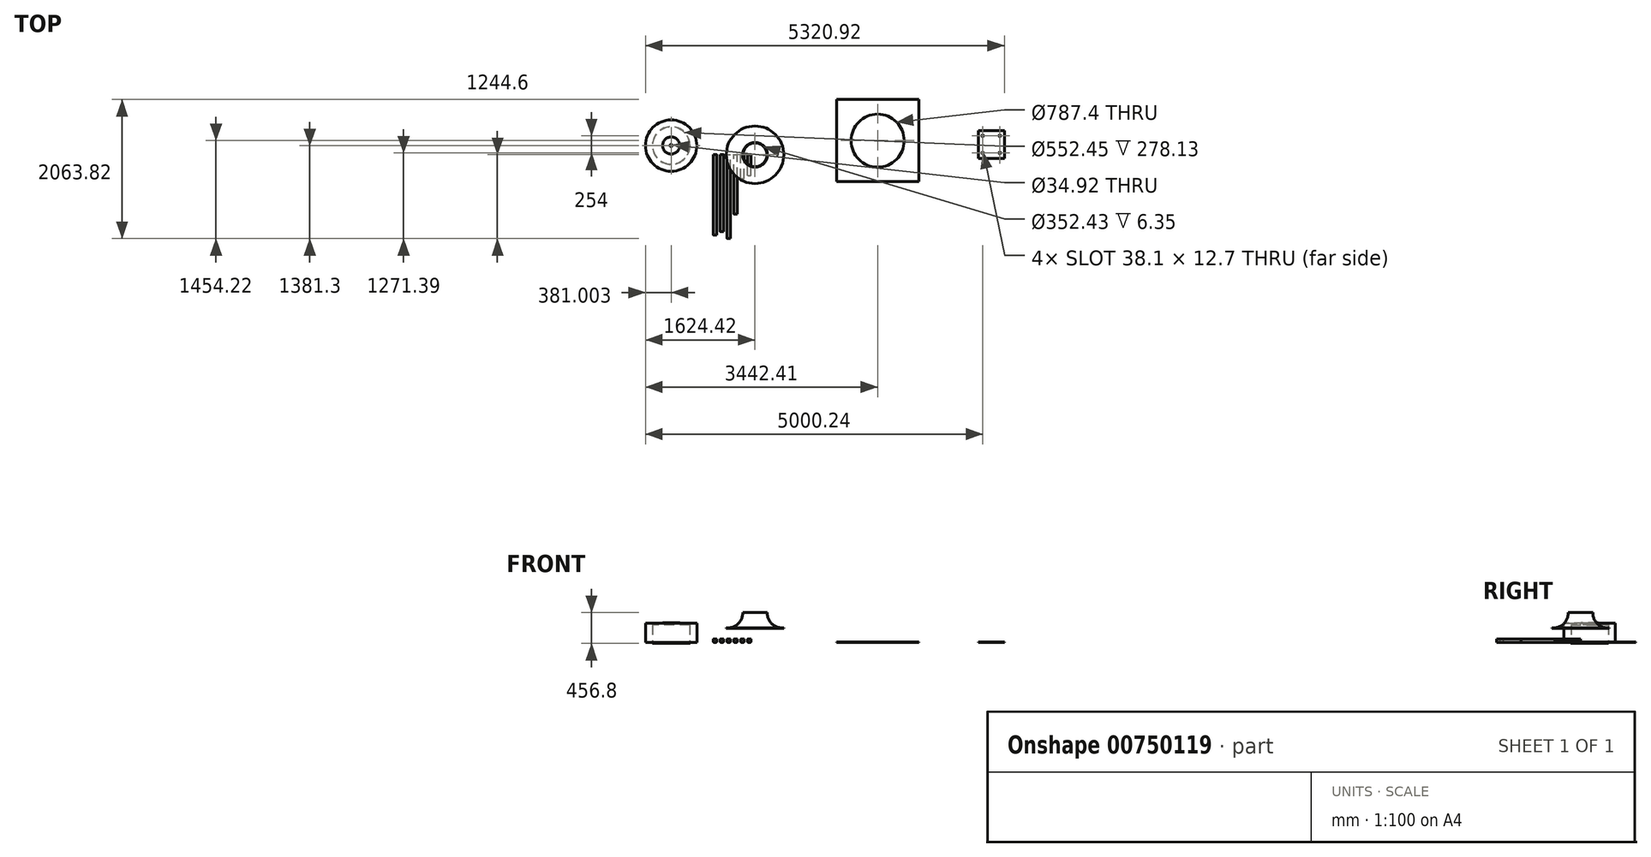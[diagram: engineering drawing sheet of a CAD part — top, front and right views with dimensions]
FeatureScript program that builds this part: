
annotation { "Feature Type Name" : "Feature", "Feature Type Description" : "" }
export const myFeature = defineFeature(function(context is Context, id is Id, definition is map)
    precondition{}
    {
        {
            var Q0;
            Q0=qCreatedBy(makeId("Front.planeOp"),FACE);
            var sketch = newSketch(context, id + "F0", { "sketchPlane" : qUnion([Q0])});
            skLineSegment(sketch, "E0.bottom", {"start": v(0, 0) * mm, "end": v(50.8, 0) * mm});
            skLineSegment(sketch, "E0.top", {"start": v(0, 50.8) * mm, "end": v(50.8, 50.8) * mm});
            skLineSegment(sketch, "E0.left", {"start": v(0, 0) * mm, "end": v(0, 50.8) * mm});
            skLineSegment(sketch, "E0.right", {"start": v(50.8, 0) * mm, "end": v(50.8, 50.8) * mm});
            skLineSegment(sketch, "E1.1.0.0", {"start": v(101.6, 0) * mm, "end": v(101.6, 50.8) * mm});
            skLineSegment(sketch, "E1.1.0.1", {"start": v(101.6, 50.8) * mm, "end": v(152.4, 50.8) * mm});
            skLineSegment(sketch, "E1.1.0.2", {"start": v(152.4, 0) * mm, "end": v(152.4, 50.8) * mm});
            skLineSegment(sketch, "E1.1.0.3", {"start": v(101.6, 0) * mm, "end": v(152.4, 0) * mm});
            skLineSegment(sketch, "E1.2.0.0", {"start": v(203.2, 0) * mm, "end": v(203.2, 50.8) * mm});
            skLineSegment(sketch, "E1.2.0.1", {"start": v(203.2, 50.8) * mm, "end": v(254, 50.8) * mm});
            skLineSegment(sketch, "E1.2.0.2", {"start": v(254, 0) * mm, "end": v(254, 50.8) * mm});
            skLineSegment(sketch, "E1.2.0.3", {"start": v(203.2, 0) * mm, "end": v(254, 0) * mm});
            skLineSegment(sketch, "E1.3.0.0", {"start": v(304.8, 0) * mm, "end": v(304.8, 50.8) * mm});
            skLineSegment(sketch, "E1.3.0.1", {"start": v(304.8, 50.8) * mm, "end": v(355.6, 50.8) * mm});
            skLineSegment(sketch, "E1.3.0.2", {"start": v(355.6, 0) * mm, "end": v(355.6, 50.8) * mm});
            skLineSegment(sketch, "E1.3.0.3", {"start": v(304.8, 0) * mm, "end": v(355.6, 0) * mm});
            skLineSegment(sketch, "E1.4.0.0", {"start": v(406.4, 0) * mm, "end": v(406.4, 50.8) * mm});
            skLineSegment(sketch, "E1.4.0.1", {"start": v(406.4, 50.8) * mm, "end": v(457.2, 50.8) * mm});
            skLineSegment(sketch, "E1.4.0.2", {"start": v(457.2, 0) * mm, "end": v(457.2, 50.8) * mm});
            skLineSegment(sketch, "E1.4.0.3", {"start": v(406.4, 0) * mm, "end": v(457.2, 0) * mm});
            skLineSegment(sketch, "E1.5.0.0", {"start": v(508, 0) * mm, "end": v(508, 50.8) * mm});
            skLineSegment(sketch, "E1.5.0.1", {"start": v(508, 50.8) * mm, "end": v(558.8, 50.8) * mm});
            skLineSegment(sketch, "E1.5.0.2", {"start": v(558.8, 0) * mm, "end": v(558.8, 50.8) * mm});
            skLineSegment(sketch, "E1.5.0.3", {"start": v(508, 0) * mm, "end": v(558.8, 0) * mm});
            skLineSegment(sketch, "E1.6.0.0", {"start": v(609.6, 0) * mm, "end": v(609.6, 50.8) * mm});
            skLineSegment(sketch, "E1.6.0.1", {"start": v(609.6, 50.8) * mm, "end": v(660.4, 50.8) * mm});
            skLineSegment(sketch, "E1.6.0.2", {"start": v(660.4, 0) * mm, "end": v(660.4, 50.8) * mm});
            skLineSegment(sketch, "E1.6.0.3", {"start": v(609.6, 0) * mm, "end": v(660.4, 0) * mm});
            skLineSegment(sketch, "E1.7.0.0", {"start": v(711.2, 0) * mm, "end": v(711.2, 50.8) * mm});
            skLineSegment(sketch, "E1.7.0.1", {"start": v(711.2, 50.8) * mm, "end": v(762, 50.8) * mm});
            skLineSegment(sketch, "E1.7.0.2", {"start": v(762, 0) * mm, "end": v(762, 50.8) * mm});
            skLineSegment(sketch, "E1.7.0.3", {"start": v(711.2, 0) * mm, "end": v(762, 0) * mm});
            skLineSegment(sketch, "E1.8.0.0", {"start": v(812.8, 0) * mm, "end": v(812.8, 50.8) * mm});
            skLineSegment(sketch, "E1.8.0.1", {"start": v(812.8, 50.8) * mm, "end": v(863.6, 50.8) * mm});
            skLineSegment(sketch, "E1.8.0.2", {"start": v(863.6, 0) * mm, "end": v(863.6, 50.8) * mm});
            skLineSegment(sketch, "E1.8.0.3", {"start": v(812.8, 0) * mm, "end": v(863.6, 0) * mm});
            skLineSegment(sketch, "E1.9.0.0", {"start": v(914.4, 0) * mm, "end": v(914.4, 50.8) * mm});
            skLineSegment(sketch, "E1.9.0.1", {"start": v(914.4, 50.8) * mm, "end": v(965.2, 50.8) * mm});
            skLineSegment(sketch, "E1.9.0.2", {"start": v(965.2, 0) * mm, "end": v(965.2, 50.8) * mm});
            skLineSegment(sketch, "E1.9.0.3", {"start": v(914.4, 0) * mm, "end": v(965.2, 0) * mm});
            skLineSegment(sketch, "E1.direction1", {"start": v(0, 0) * mm, "end": v(101.6, 0) * mm, "construction": true});
            skSolve(sketch);
        }
        {
            var Q0;
            Q0=makeQuery(id+"F0.imprint","IMPRINT",FACE,{"disambiguationData":[TD([[makeQuery(id+"F0.imprint","IMPRINT",EDGE,{"derivedFrom":sQuery(id+"F0.wireOp",EDGE,"E0.bottom")}),1.0]])]});
            extrude(context, id + "F1", {"entities" : qUnion([Q0]), "depth" : 1193.8 * mm, "offsetDistance" : 25.4 * mm});
        }
        {
            var Q0;
            Q0=makeQuery(id+"F1.opExtrude","SWEPT_EDGE",EDGE,{"disambiguationData":[OSD([sQuery(id+"F0.wireOp",EDGE,"E0.top"),sQuery(id+"F0.wireOp",EDGE,"E0.left")])]});
            var Q1;
            Q1=makeQuery(id+"F1.opExtrude","SWEPT_EDGE",EDGE,{"disambiguationData":[OSD([sQuery(id+"F0.wireOp",EDGE,"E0.bottom"),sQuery(id+"F0.wireOp",EDGE,"E0.left")])]});
            var Q2;
            Q2=makeQuery(id+"F1.opExtrude","SWEPT_EDGE",EDGE,{"disambiguationData":[OSD([sQuery(id+"F0.wireOp",EDGE,"E0.top"),sQuery(id+"F0.wireOp",EDGE,"E0.right")])]});
            var Q3;
            Q3=makeQuery(id+"F1.opExtrude","SWEPT_EDGE",EDGE,{"disambiguationData":[OSD([sQuery(id+"F0.wireOp",EDGE,"E0.bottom"),sQuery(id+"F0.wireOp",EDGE,"E0.right")])]});
            fillet(context, id + "F2", {"entities" : qUnion([Q0, Q1, Q2, Q3]), "radius" : 6.35 * mm, "tangentPropagation" : true, "allowEdgeOverflow" : false});
        }
        {
            var Q0;
            Q0=makeQuery(id+"F0.imprint","IMPRINT",FACE,{"disambiguationData":[TD([[makeQuery(id+"F0.imprint","IMPRINT",EDGE,{"derivedFrom":sQuery(id+"F0.wireOp",EDGE,"E1.1.0.0")}),-1.0]])]});
            extrude(context, id + "F3", {"entities" : qUnion([Q0]), "depth" : 1143 * mm, "offsetDistance" : 25.4 * mm});
        }
        {
            var Q0;
            Q0=makeQuery(id+"F0.imprint","IMPRINT",FACE,{"disambiguationData":[TD([[makeQuery(id+"F0.imprint","IMPRINT",EDGE,{"derivedFrom":sQuery(id+"F0.wireOp",EDGE,"E1.2.0.0")}),-1.0]])]});
            extrude(context, id + "F4", {"entities" : qUnion([Q0]), "depth" : 1244.6 * mm, "offsetDistance" : 25.4 * mm});
        }
        {
            var Q0;
            Q0=makeQuery(id+"F0.imprint","IMPRINT",FACE,{"disambiguationData":[TD([[makeQuery(id+"F0.imprint","IMPRINT",EDGE,{"derivedFrom":sQuery(id+"F0.wireOp",EDGE,"E1.3.0.0")}),-1.0]])]});
            extrude(context, id + "F5", {"entities" : qUnion([Q0]), "depth" : 882.65 * mm, "offsetDistance" : 25.4 * mm});
        }
        {
            var Q0;
            Q0=makeQuery(id+"F0.imprint","IMPRINT",FACE,{"disambiguationData":[TD([[makeQuery(id+"F0.imprint","IMPRINT",EDGE,{"derivedFrom":sQuery(id+"F0.wireOp",EDGE,"E1.4.0.0")}),-1.0]])]});
            extrude(context, id + "F6", {"entities" : qUnion([Q0]), "depth" : 355.6 * mm, "offsetDistance" : 25.4 * mm});
        }
        {
            var Q0;
            Q0=qCreatedBy(makeId("Front.planeOp"),FACE);
            var sketch = newSketch(context, id + "F7", { "sketchPlane" : qUnion([Q0])});
            skLineSegment(sketch, "E2", {"start": v(191.08, 213.6) * mm, "end": v(216.48, 213.6) * mm});
            skArc(sketch, "E3", {"start": v(216.48, 213.6) * mm, "mid": v(371.4, 277.76) * mm, "end": v(435.56, 432.67) * mm});
            skLineSegment(sketch, "E4", {"start": v(435.56, 432.67) * mm, "end": v(435.56, 439.02) * mm});
            skLineSegment(sketch, "E5", {"start": v(618.12, 554.37) * mm, "end": v(618.12, 107.04) * mm, "construction": true});
            skLineSegment(sketch, "E6.0", {"start": v(441.9, 432.67) * mm, "end": v(441.9, 439.02) * mm});
            skArc(sketch, "E6.1", {"start": v(216.48, 207.24) * mm, "mid": v(375.88, 273.27) * mm, "end": v(441.9, 432.67) * mm});
            skLineSegment(sketch, "E6.2", {"start": v(191.08, 207.24) * mm, "end": v(216.48, 207.24) * mm});
            skLineSegment(sketch, "E7", {"start": v(435.56, 439.02) * mm, "end": v(441.9, 439.02) * mm});
            skLineSegment(sketch, "E8", {"start": v(191.08, 213.6) * mm, "end": v(191.08, 207.24) * mm});
            skSolve(sketch);
        }
        {
            var Q0;
            Q0 = qSketchRegion(id + "F7", true);
            var Q1;
            Q1=sQuery(id+"F7.wireOp",EDGE,"E5");
            revolve(context, id + "F8", {"surfaceOperationType" : NewSurfaceOperationType.NEW, "entities" : qUnion([Q0]), "axis" : qUnion([Q1]), "revolveType" : RevolveType.FULL});
        }
        {
            var Q0;
            Q0=qCreatedBy(makeId("Top.planeOp"),FACE);
            var sketch = newSketch(context, id + "F9", { "sketchPlane" : qUnion([Q0])});
            skCircle(sketch, "E9", {"center": v(-625.3, 136.7) * mm, "radius": 381 * mm});
            skCircle(sketch, "E10", {"center": v(-625.3, 136.7) * mm, "radius": 276.23 * mm});
            skCircle(sketch, "E11", {"center": v(-625.3, 136.7) * mm, "radius": 17.46 * mm});
            skSolve(sketch);
        }
        {
            var Q0;
            Q0=makeQuery(id+"F9.imprint","IMPRINT",FACE,{"disambiguationData":[TD([[makeQuery(id+"F9.imprint","IMPRINT",EDGE,{"derivedFrom":sQuery(id+"F9.wireOp",EDGE,"E9")}),1.0]])]});
            extrude(context, id + "F10", {"entities" : qUnion([Q0]), "depth" : 285.75 * mm, "offsetDistance" : 25.4 * mm});
        }
        {
            var Q0;
            Q0=makeQuery(id+"F0.imprint","IMPRINT",FACE,{"disambiguationData":[TD([[makeQuery(id+"F0.imprint","IMPRINT",EDGE,{"derivedFrom":sQuery(id+"F0.wireOp",EDGE,"E1.5.0.0")}),-1.0]])]});
            extrude(context, id + "F11", {"entities" : qUnion([Q0]), "depth" : 311.15 * mm, "offsetDistance" : 25.4 * mm});
        }
        {
            var Q0;
            Q0=qCreatedBy(makeId("Top.planeOp"),FACE);
            var sketch = newSketch(context, id + "F12", { "sketchPlane" : qUnion([Q0])});
            skLineSegment(sketch, "E12.bottom", {"start": v(1826.5, 819.22) * mm, "end": v(3045.7, 819.22) * mm});
            skLineSegment(sketch, "E12.top", {"start": v(1826.5, -399.98) * mm, "end": v(3045.7, -399.98) * mm});
            skLineSegment(sketch, "E12.left", {"start": v(1826.5, 819.22) * mm, "end": v(1826.5, -399.98) * mm});
            skLineSegment(sketch, "E12.right", {"start": v(3045.7, 819.22) * mm, "end": v(3045.7, -399.98) * mm});
            skCircle(sketch, "E13", {"center": v(2436.1, 209.62) * mm, "radius": 393.7 * mm});
            skPoint(sketch, "E13.centerSnap0", {"position": v(2436.1, 819.22) * mm});
            skPoint(sketch, "E13.centerSnap1", {"position": v(1826.5, 209.62) * mm});
            skSolve(sketch);
        }
        {
            var Q0;
            Q0 = qSketchRegion(id + "F12", true);
            extrude(context, id + "F13", {"entities" : qUnion([Q0]), "depth" : 3.17 * mm, "offsetDistance" : 25.4 * mm});
        }
        {
            var Q0;
            Q0=qCreatedBy(makeId("Top.planeOp"),FACE);
            var sketch = newSketch(context, id + "F14", { "sketchPlane" : qUnion([Q0])});
            skLineSegment(sketch, "E14.bottom", {"start": v(3927.27, 360.16) * mm, "end": v(4314.62, 360.16) * mm});
            skLineSegment(sketch, "E14.top", {"start": v(3927.27, -52.59) * mm, "end": v(4314.62, -52.59) * mm});
            skLineSegment(sketch, "E14.left", {"start": v(3927.27, 360.16) * mm, "end": v(3927.27, -52.59) * mm});
            skLineSegment(sketch, "E14.right", {"start": v(4314.62, 360.16) * mm, "end": v(4314.62, -52.59) * mm});
            skLineSegment(sketch, "E15", {"start": v(3978.07, 309.36) * mm, "end": v(3978.07, -1.79) * mm, "construction": true});
            skLineSegment(sketch, "E16", {"start": v(3978.07, -1.79) * mm, "end": v(4263.82, -1.79) * mm, "construction": true});
            skLineSegment(sketch, "E17", {"start": v(4263.82, -1.79) * mm, "end": v(4263.82, 309.36) * mm, "construction": true});
            skLineSegment(sketch, "E18", {"start": v(4263.82, 309.36) * mm, "end": v(3978.07, 309.36) * mm, "construction": true});
            skLineSegment(sketch, "E19", {"start": v(3993.94, 293.49) * mm, "end": v(3993.94, 268.09) * mm});
            skLineSegment(sketch, "E20", {"start": v(4247.94, 293.49) * mm, "end": v(4247.94, 268.09) * mm});
            skLineSegment(sketch, "E21", {"start": v(3993.94, 39.49) * mm, "end": v(3993.94, 14.09) * mm});
            skLineSegment(sketch, "E22", {"start": v(4247.94, 39.49) * mm, "end": v(4247.94, 14.09) * mm});
            skLineSegment(sketch, "E23", {"start": v(4120.94, 360.16) * mm, "end": v(4120.94, -52.59) * mm, "construction": true});
            skArc(sketch, "E24.0.startCap", {"start": v(3987.6, 293.49) * mm, "mid": v(3993.94, 299.84) * mm, "end": v(4000.3, 293.49) * mm});
            skArc(sketch, "E24.0.endCap", {"start": v(4000.3, 268.09) * mm, "mid": v(3993.94, 261.74) * mm, "end": v(3987.6, 268.09) * mm});
            skLineSegment(sketch, "E24.0.left", {"start": v(4000.3, 293.49) * mm, "end": v(4000.3, 268.09) * mm});
            skLineSegment(sketch, "E24.0.right", {"start": v(3987.6, 293.49) * mm, "end": v(3987.6, 268.09) * mm});
            skArc(sketch, "E24.1.startCap", {"start": v(4241.6, 293.49) * mm, "mid": v(4247.94, 299.84) * mm, "end": v(4254.3, 293.49) * mm});
            skArc(sketch, "E24.1.endCap", {"start": v(4254.3, 268.09) * mm, "mid": v(4247.94, 261.74) * mm, "end": v(4241.6, 268.09) * mm});
            skLineSegment(sketch, "E24.1.left", {"start": v(4254.3, 293.49) * mm, "end": v(4254.3, 268.09) * mm});
            skLineSegment(sketch, "E24.1.right", {"start": v(4241.6, 293.49) * mm, "end": v(4241.6, 268.09) * mm});
            skArc(sketch, "E24.2.startCap", {"start": v(4241.6, 39.49) * mm, "mid": v(4247.94, 45.84) * mm, "end": v(4254.3, 39.49) * mm});
            skArc(sketch, "E24.2.endCap", {"start": v(4254.3, 14.09) * mm, "mid": v(4247.94, 7.74) * mm, "end": v(4241.6, 14.09) * mm});
            skLineSegment(sketch, "E24.2.left", {"start": v(4254.3, 39.49) * mm, "end": v(4254.3, 14.09) * mm});
            skLineSegment(sketch, "E24.2.right", {"start": v(4241.6, 39.49) * mm, "end": v(4241.6, 14.09) * mm});
            skArc(sketch, "E24.3.startCap", {"start": v(3987.6, 39.49) * mm, "mid": v(3993.94, 45.84) * mm, "end": v(4000.3, 39.49) * mm});
            skArc(sketch, "E24.3.endCap", {"start": v(4000.3, 14.09) * mm, "mid": v(3993.94, 7.74) * mm, "end": v(3987.6, 14.09) * mm});
            skLineSegment(sketch, "E24.3.left", {"start": v(4000.3, 39.49) * mm, "end": v(4000.3, 14.09) * mm});
            skLineSegment(sketch, "E24.3.right", {"start": v(3987.6, 39.49) * mm, "end": v(3987.6, 14.09) * mm});
            skPoint(sketch, "E25", {"position": v(4247.94, 280.79) * mm});
            skPoint(sketch, "E26", {"position": v(3993.94, 280.79) * mm});
            skPoint(sketch, "E27", {"position": v(3993.94, 26.79) * mm});
            skPoint(sketch, "E28", {"position": v(4247.94, 26.79) * mm});
            skSolve(sketch);
        }
        {
            var Q0;
            Q0 = qSketchRegion(id + "F14", true);
            extrude(context, id + "F15", {"entities" : qUnion([Q0]), "depth" : 6.35 * mm, "offsetDistance" : 25.4 * mm});
        }
        {
            var Q0;
            Q0=makeQuery(id+"F3.opExtrude","SWEPT_EDGE",EDGE,{"disambiguationData":[OSD([sQuery(id+"F0.wireOp",EDGE,"E1.1.0.0"),sQuery(id+"F0.wireOp",EDGE,"E1.1.0.1")])]});
            var Q1;
            Q1=makeQuery(id+"F3.opExtrude","SWEPT_EDGE",EDGE,{"disambiguationData":[OSD([sQuery(id+"F0.wireOp",EDGE,"E1.1.0.1"),sQuery(id+"F0.wireOp",EDGE,"E1.1.0.2")])]});
            var Q2;
            Q2=makeQuery(id+"F4.opExtrude","SWEPT_EDGE",EDGE,{"disambiguationData":[OSD([sQuery(id+"F0.wireOp",EDGE,"E1.2.0.0"),sQuery(id+"F0.wireOp",EDGE,"E1.2.0.1")])]});
            var Q3;
            Q3=makeQuery(id+"F4.opExtrude","SWEPT_EDGE",EDGE,{"disambiguationData":[OSD([sQuery(id+"F0.wireOp",EDGE,"E1.2.0.1"),sQuery(id+"F0.wireOp",EDGE,"E1.2.0.2")])]});
            var Q4;
            Q4=makeQuery(id+"F3.opExtrude","SWEPT_EDGE",EDGE,{"disambiguationData":[OSD([sQuery(id+"F0.wireOp",EDGE,"E1.1.0.0"),sQuery(id+"F0.wireOp",EDGE,"E1.1.0.3")])]});
            var Q5;
            Q5=makeQuery(id+"F3.opExtrude","SWEPT_EDGE",EDGE,{"disambiguationData":[OSD([sQuery(id+"F0.wireOp",EDGE,"E1.1.0.2"),sQuery(id+"F0.wireOp",EDGE,"E1.1.0.3")])]});
            var Q6;
            Q6=makeQuery(id+"F4.opExtrude","SWEPT_EDGE",EDGE,{"disambiguationData":[OSD([sQuery(id+"F0.wireOp",EDGE,"E1.2.0.0"),sQuery(id+"F0.wireOp",EDGE,"E1.2.0.3")])]});
            var Q7;
            Q7=makeQuery(id+"F4.opExtrude","SWEPT_EDGE",EDGE,{"disambiguationData":[OSD([sQuery(id+"F0.wireOp",EDGE,"E1.2.0.2"),sQuery(id+"F0.wireOp",EDGE,"E1.2.0.3")])]});
            var Q8;
            Q8=makeQuery(id+"F5.opExtrude","SWEPT_EDGE",EDGE,{"disambiguationData":[OSD([sQuery(id+"F0.wireOp",EDGE,"E1.3.0.0"),sQuery(id+"F0.wireOp",EDGE,"E1.3.0.3")])]});
            var Q9;
            Q9=makeQuery(id+"F5.opExtrude","SWEPT_EDGE",EDGE,{"disambiguationData":[OSD([sQuery(id+"F0.wireOp",EDGE,"E1.3.0.2"),sQuery(id+"F0.wireOp",EDGE,"E1.3.0.3")])]});
            var Q10;
            Q10=makeQuery(id+"F6.opExtrude","SWEPT_EDGE",EDGE,{"disambiguationData":[OSD([sQuery(id+"F0.wireOp",EDGE,"E1.4.0.0"),sQuery(id+"F0.wireOp",EDGE,"E1.4.0.3")])]});
            var Q11;
            Q11=makeQuery(id+"F6.opExtrude","SWEPT_EDGE",EDGE,{"disambiguationData":[OSD([sQuery(id+"F0.wireOp",EDGE,"E1.4.0.2"),sQuery(id+"F0.wireOp",EDGE,"E1.4.0.3")])]});
            var Q12;
            Q12=makeQuery(id+"F11.opExtrude","SWEPT_EDGE",EDGE,{"disambiguationData":[OSD([sQuery(id+"F0.wireOp",EDGE,"E1.5.0.0"),sQuery(id+"F0.wireOp",EDGE,"E1.5.0.3")])]});
            var Q13;
            Q13=makeQuery(id+"F11.opExtrude","SWEPT_EDGE",EDGE,{"disambiguationData":[OSD([sQuery(id+"F0.wireOp",EDGE,"E1.5.0.2"),sQuery(id+"F0.wireOp",EDGE,"E1.5.0.3")])]});
            var Q14;
            Q14=makeQuery(id+"F5.opExtrude","SWEPT_EDGE",EDGE,{"disambiguationData":[OSD([sQuery(id+"F0.wireOp",EDGE,"E1.3.0.0"),sQuery(id+"F0.wireOp",EDGE,"E1.3.0.1")])]});
            var Q15;
            Q15=makeQuery(id+"F5.opExtrude","SWEPT_EDGE",EDGE,{"disambiguationData":[OSD([sQuery(id+"F0.wireOp",EDGE,"E1.3.0.1"),sQuery(id+"F0.wireOp",EDGE,"E1.3.0.2")])]});
            var Q16;
            Q16=makeQuery(id+"F6.opExtrude","SWEPT_EDGE",EDGE,{"disambiguationData":[OSD([sQuery(id+"F0.wireOp",EDGE,"E1.4.0.0"),sQuery(id+"F0.wireOp",EDGE,"E1.4.0.1")])]});
            var Q17;
            Q17=makeQuery(id+"F6.opExtrude","SWEPT_EDGE",EDGE,{"disambiguationData":[OSD([sQuery(id+"F0.wireOp",EDGE,"E1.4.0.1"),sQuery(id+"F0.wireOp",EDGE,"E1.4.0.2")])]});
            var Q18;
            Q18=makeQuery(id+"F11.opExtrude","SWEPT_EDGE",EDGE,{"disambiguationData":[OSD([sQuery(id+"F0.wireOp",EDGE,"E1.5.0.0"),sQuery(id+"F0.wireOp",EDGE,"E1.5.0.1")])]});
            var Q19;
            Q19=makeQuery(id+"F11.opExtrude","SWEPT_EDGE",EDGE,{"disambiguationData":[OSD([sQuery(id+"F0.wireOp",EDGE,"E1.5.0.1"),sQuery(id+"F0.wireOp",EDGE,"E1.5.0.2")])]});
            fillet(context, id + "F16", {"entities" : qUnion([Q0, Q1, Q2, Q3, Q4, Q5, Q6, Q7, Q8, Q9, Q10, Q11, Q12, Q13, Q14, Q15, Q16, Q17, Q18, Q19]), "radius" : 6.35 * mm, "tangentPropagation" : true, "allowEdgeOverflow" : false});
        }
        {
            var Q0;
            Q0=makeQuery(id+"F10.opExtrude","CAP_FACE",FACE,{"disambiguationData":[OSD([sQuery(id+"F9.wireOp",EDGE,"E9"),sQuery(id+"F9.wireOp",EDGE,"E10")])],"isStart":false});
            var sketch = newSketch(context, id + "F17", { "sketchPlane" : qUnion([Q0])});
            skCircle(sketch, "E29", {"center": v(-625.3, 136.7) * mm, "radius": 276.23 * mm});
            skSolve(sketch);
        }
        {
            var Q0;
            Q0=makeQuery(id+"F17.imprint","IMPRINT",FACE,{"disambiguationData":[TD([[makeQuery(id+"F17.imprint","IMPRINT",EDGE,{"derivedFrom":sQuery(id+"F17.wireOp",EDGE,"E29")}),1.0]])]});
            extrude(context, id + "F18", {"entities" : qUnion([Q0]), "operationType" : NewBodyOperationType.ADD, "oppositeDirection" : true, "depth" : 25.4 * mm, "offsetDistance" : 25.4 * mm});
        }
        {
            var Q0;
            Q0=makeQuery(id+"F18.boolean.opBoolean","MERGE",FACE,{"derivedFrom":[makeQuery(id+"F10.opExtrude","CAP_FACE",FACE,{"disambiguationData":[OSD([sQuery(id+"F9.wireOp",EDGE,"E9"),sQuery(id+"F9.wireOp",EDGE,"E10")])],"isStart":false}),makeQuery(id+"F18.opExtrude","CAP_FACE",FACE,{"disambiguationData":[OSD([sQuery(id+"F17.wireOp",EDGE,"E29")])],"isStart":true})]});
            var sketch = newSketch(context, id + "F19", { "sketchPlane" : qUnion([Q0])});
            skCircle(sketch, "E30", {"center": v(-625.3, 136.7) * mm, "radius": 17.46 * mm});
            skSolve(sketch);
        }
        {
            var Q0;
            Q0=makeQuery(id+"F19.imprint","IMPRINT",FACE,{"disambiguationData":[TD([[makeQuery(id+"F19.imprint","IMPRINT",EDGE,{"derivedFrom":sQuery(id+"F19.wireOp",EDGE,"E30")}),1.0]])]});
            extrude(context, id + "F20", {"entities" : qUnion([Q0]), "operationType" : NewBodyOperationType.REMOVE, "endBound" : BoundingType.UP_TO_NEXT, "oppositeDirection" : true, "depth" : 25.4 * mm, "offsetDistance" : 25.4 * mm});
        }
        {
            var Q0;
            Q0=makeQuery(id+"F18.boolean.opBoolean","MERGE",FACE,{"derivedFrom":[makeQuery(id+"F10.opExtrude","CAP_FACE",FACE,{"disambiguationData":[OSD([sQuery(id+"F9.wireOp",EDGE,"E9"),sQuery(id+"F9.wireOp",EDGE,"E10")])],"isStart":false}),makeQuery(id+"F18.opExtrude","CAP_FACE",FACE,{"disambiguationData":[OSD([sQuery(id+"F17.wireOp",EDGE,"E29")])],"isStart":true})]});
            var sketch = newSketch(context, id + "F21", { "sketchPlane" : qUnion([Q0])});
            skCircle(sketch, "E31", {"center": v(-625.3, 136.7) * mm, "radius": 127 * mm});
            skSolve(sketch);
        }
        {
            var Q0;
            Q0=makeQuery(id+"F21.imprint","IMPRINT",FACE,{"disambiguationData":[TD([[makeQuery(id+"F21.imprint","IMPRINT",EDGE,{"derivedFrom":sQuery(id+"F21.wireOp",EDGE,"E31")}),1.0]])]});
            extrude(context, id + "F22", {"entities" : qUnion([Q0]), "operationType" : NewBodyOperationType.ADD, "depth" : 6.35 * mm, "offsetDistance" : 25.4 * mm});
        }
        {
            var Q0;
            Q0=makeQuery(id+"F10.opExtrude","CAP_FACE",FACE,{"disambiguationData":[OSD([sQuery(id+"F9.wireOp",EDGE,"E9"),sQuery(id+"F9.wireOp",EDGE,"E10")])],"isStart":true});
            var sketch = newSketch(context, id + "F23", { "sketchPlane" : qUnion([Q0])});
            skCircle(sketch, "E32", {"center": v(-625.3, -136.7) * mm, "radius": 279.4 * mm});
            skSolve(sketch);
        }
        {
            var Q0;
            Q0=makeQuery(id+"F23.imprint","IMPRINT",FACE,{"disambiguationData":[TD([[makeQuery(id+"F23.imprint","IMPRINT",EDGE,{"derivedFrom":sQuery(id+"F23.wireOp",EDGE,"E32")}),1.0]])]});
            extrude(context, id + "F24", {"entities" : qUnion([Q0]), "operationType" : NewBodyOperationType.ADD, "depth" : 17.78 * mm, "offsetDistance" : 25.4 * mm});
        }
    });
